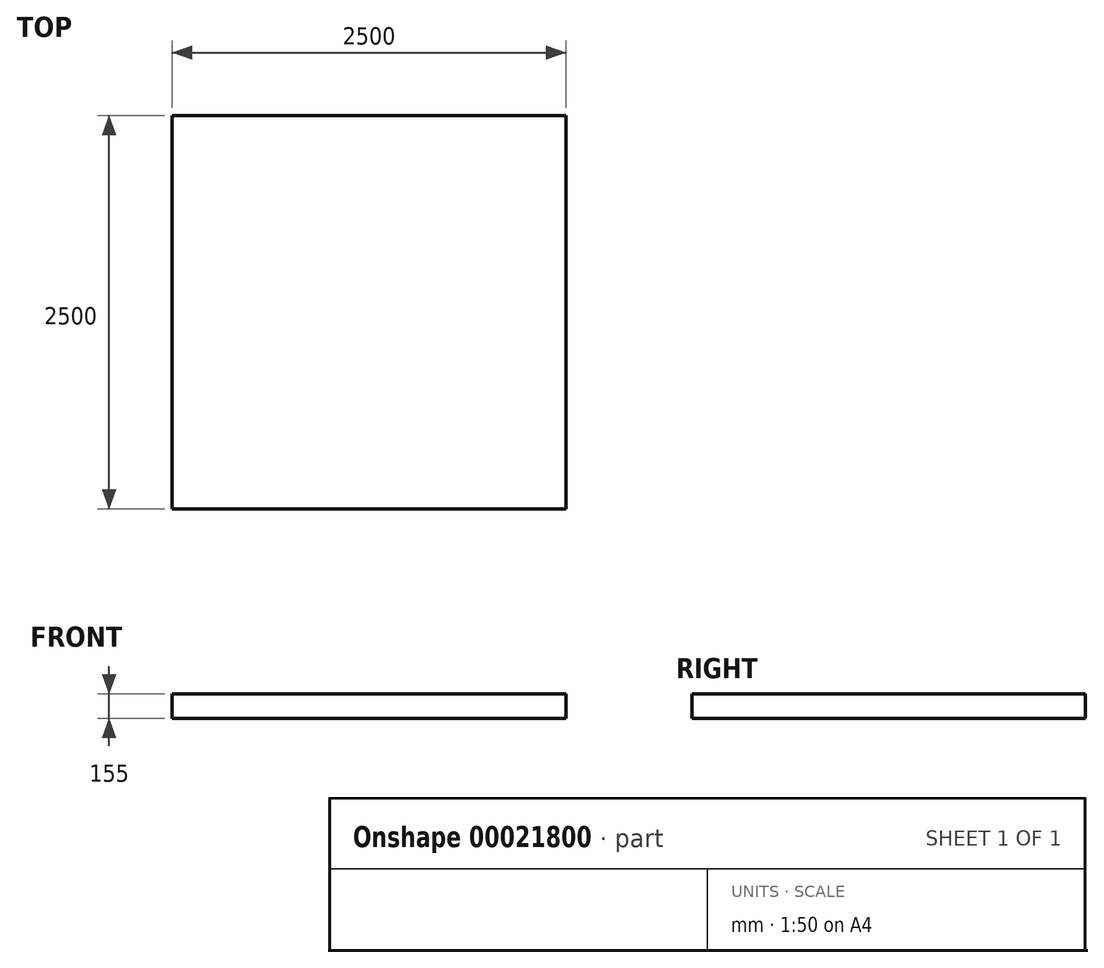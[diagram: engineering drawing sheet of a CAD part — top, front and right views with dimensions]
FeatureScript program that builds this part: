
annotation { "Feature Type Name" : "Feature", "Feature Type Description" : "" }
export const myFeature = defineFeature(function(context is Context, id is Id, definition is map)
    precondition{}
    {
        {
            var Q0;
            Q0=qCreatedBy(makeId("Top.planeOp"),FACE);
            var sketch = newSketch(context, id + "F0", { "sketchPlane" : qUnion([Q0])});
            skLineSegment(sketch, "E0.rect.bottom", {"start": v(-1250, -1250) * mm, "end": v(1250, -1250) * mm});
            skLineSegment(sketch, "E0.rect.top", {"start": v(-1250, 1250) * mm, "end": v(1250, 1250) * mm});
            skLineSegment(sketch, "E0.rect.left", {"start": v(-1250, -1250) * mm, "end": v(-1250, 1250) * mm});
            skLineSegment(sketch, "E0.rect.right", {"start": v(1250, -1250) * mm, "end": v(1250, 1250) * mm});
            skPoint(sketch, "E0.rect.middle", {"position": v(0, 0) * mm});
            skSolve(sketch);
        }
        {
            var Q0;
            Q0=makeQuery(id+"F0.imprint","IMPRINT",FACE,{"disambiguationData":[TD([[makeQuery(id+"F0.imprint","IMPRINT",EDGE,{"derivedFrom":sQuery(id+"F0.wireOp",EDGE,"E0.rect.bottom")}),1.0]])]});
            extrude(context, id + "F1", {"entities" : qUnion([Q0]), "depth" : 155 * mm});
        }
    });
